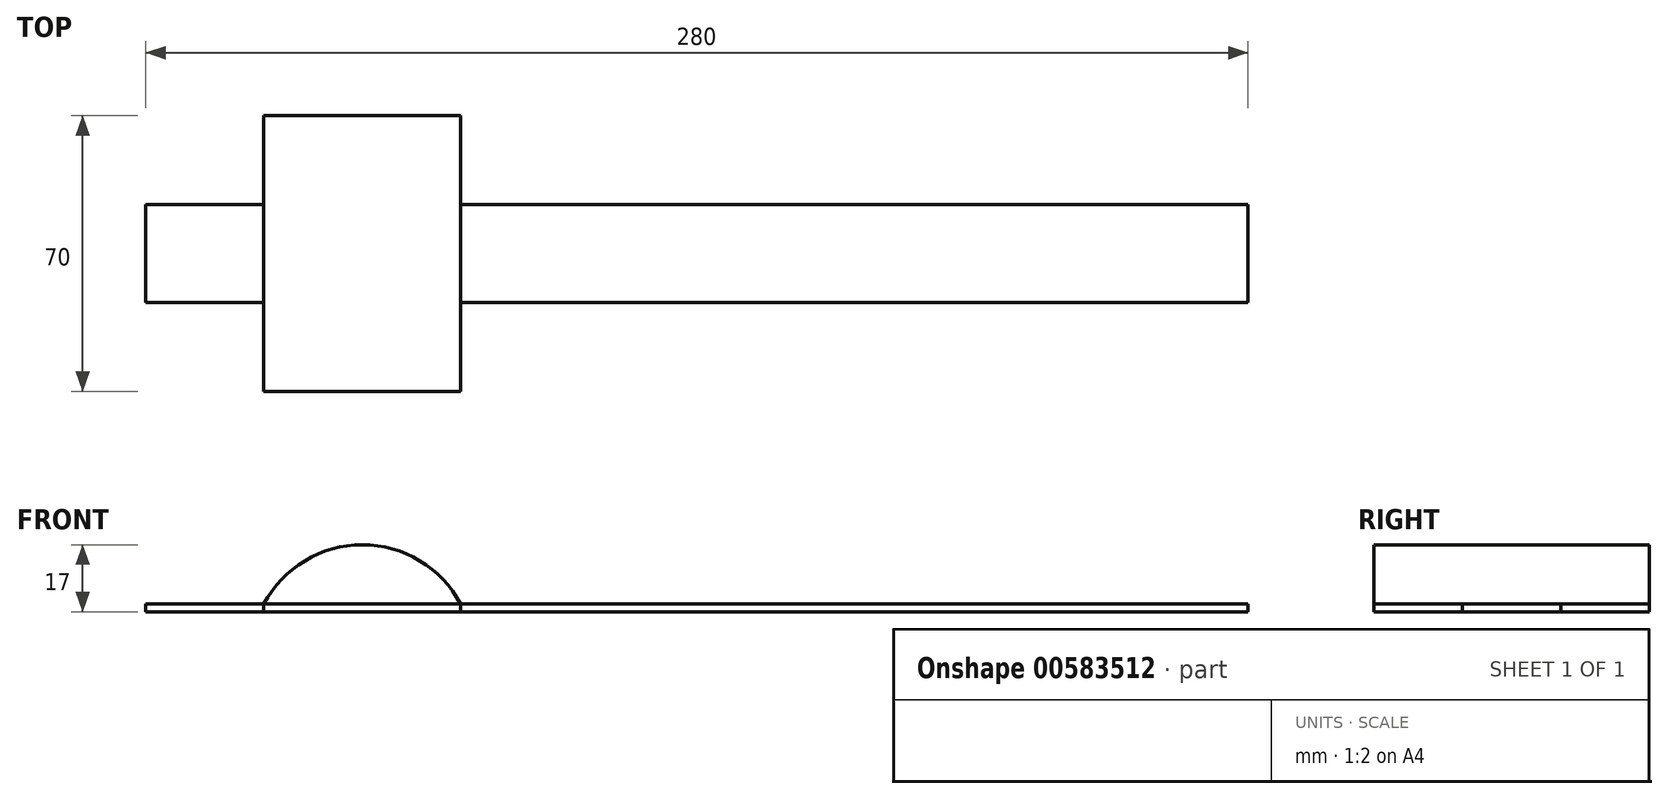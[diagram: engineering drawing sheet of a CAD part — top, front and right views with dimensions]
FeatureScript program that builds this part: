
annotation { "Feature Type Name" : "Feature", "Feature Type Description" : "" }
export const myFeature = defineFeature(function(context is Context, id is Id, definition is map)
    precondition{}
    {
        {
            var Q0;
            Q0=qCreatedBy(makeId("Top.planeOp"),FACE);
            var sketch = newSketch(context, id + "F0", { "sketchPlane" : qUnion([Q0])});
            skLineSegment(sketch, "E0.bottom", {"start": v(25, 35) * mm, "end": v(-25, 35) * mm});
            skLineSegment(sketch, "E0.top", {"start": v(25, -35) * mm, "end": v(-25, -35) * mm});
            skPoint(sketch, "E0.middle", {"position": v(0, 0) * mm});
            skLineSegment(sketch, "E1", {"start": v(25, 15) * mm, "end": v(25, 35) * mm});
            skLineSegment(sketch, "E2", {"start": v(25, -15) * mm, "end": v(25, -35) * mm});
            skLineSegment(sketch, "E3", {"start": v(-25, -35) * mm, "end": v(-25, -15) * mm});
            skLineSegment(sketch, "E4", {"start": v(-25, 35) * mm, "end": v(-25, 15) * mm});
            skLineSegment(sketch, "E5", {"start": v(-25, -15) * mm, "end": v(-25, -35) * mm});
            skLineSegment(sketch, "E6", {"start": v(-25, 12.5) * mm, "end": v(-55, 12.5) * mm});
            skLineSegment(sketch, "E7", {"start": v(-25, -12.5) * mm, "end": v(-55, -12.5) * mm});
            skLineSegment(sketch, "E8", {"start": v(-55, -12.5) * mm, "end": v(-55, 12.5) * mm});
            skLineSegment(sketch, "E9", {"start": v(-25, 12.5) * mm, "end": v(-25, 15) * mm});
            skLineSegment(sketch, "E10", {"start": v(-25, -12.5) * mm, "end": v(-25, -15) * mm});
            skLineSegment(sketch, "E11", {"start": v(25, 12.5) * mm, "end": v(25, 15) * mm});
            skLineSegment(sketch, "E12", {"start": v(25, -12.5) * mm, "end": v(25, -15) * mm});
            skLineSegment(sketch, "E13", {"start": v(25, -12.5) * mm, "end": v(225, -12.5) * mm});
            skLineSegment(sketch, "E14", {"start": v(25, 12.5) * mm, "end": v(225, 12.5) * mm});
            skLineSegment(sketch, "E15", {"start": v(225, 12.5) * mm, "end": v(225, -12.5) * mm});
            skSolve(sketch);
        }
        {
            var Q0;
            Q0 = qSketchRegion(id + "F0", true);
            extrude(context, id + "F1", {"entities" : qUnion([Q0]), "depth" : 2 * mm, "offsetDistance" : 25.4 * mm});
        }
        {
            var Q0;
            Q0=qCreatedBy(makeId("Front.planeOp"),FACE);
            var sketch = newSketch(context, id + "F2", { "sketchPlane" : qUnion([Q0])});
            skPoint(sketch, "E16.middle", {"position": v(0, 2) * mm});
            skArc(sketch, "E17", {"start": v(25, 2) * mm, "mid": v(0, 17) * mm, "end": v(-25, 2) * mm});
            skLineSegment(sketch, "E18", {"start": v(-25, 2) * mm, "end": v(25, 2) * mm});
            skSolve(sketch);
        }
        {
            var Q0;
            Q0 = qSketchRegion(id + "F2", true);
            extrude(context, id + "F3", {"entities" : qUnion([Q0]), "depth" : 35 * mm, "offsetDistance" : 25.4 * mm, "hasSecondDirection" : true, "secondDirectionOppositeDirection" : true, "secondDirectionDepth" : 35 * mm});
        }
    });
